# Revit family: QF_BPRO_TRE 6x4_575098
name_source: partatom
category: Sonderausstattung
revit_build: Autodesk Revit 2018 (Build: 20181015_0930(x64)
units: mm (PartAtom-declared; Revit-internal decimal feet)

## family parameters
Arbeitsebenenbasiert = Nein
Beim Laden mit Abzugskörper schneiden = Nein
Bemaßung runder Anschluss = Durchmesser verwenden
Gemeinsam genutzt = Nein
Immer vertikal = Ja
Raumberechnungspunkt = Nein
Teiletyp = Normal

## types (1)
- TRE 6x4
    Artikel Nummer = 575098
    Beschreibung = TRE 6 x 4
Plattformwagen
für Eurobehälter,
inkl. Schiebegriff,
mit umlaufendem Profilrand,
Plattformgröße: 640 x 430 mm
    Beschreibung durch Hersteller analog Leistungsverzeichnislangtext = Abmessungen

Länge:			742 mm
Breite:		430 mm
Höhe:		950 mm
Plattformhöhe:		201 mm


Ausführung

Der Transportroller für Eurobehälter besteht komplett aus CNS 18/10. Die Oberfläche ist mikroliert. 
Stirnseitig befindet sich ein gebogener Schiebegriff aus 25 x 25 mm Vierkantrohr. 

Der Wagen ist fahrbar mittels rostfreien Kunststoffrollen gemäß DIN 18867-8 (4 Lenkrollen, davon 2 mit Feststeller, Rollendurchmesser 125 mm). Stoßleisten aus Kunststoff (Polyethylen) an allen vier Seiten schützen vor Beschädigung.


Technische Daten

Werkstoff:		CNS 18/10
Gewicht:		10 kg 
Gesamttragfähigkeit:	120 kg
Plattformgröße:		600 x 400 mm


Besonderheit

•	Ergonomischer Schiebegriff


Fabrikat

Hersteller:			B.PRO
Modell:	TRE 6 x 4
Best.Nr.	575 098
    CE Kennzeichnung = Ja
    Gerätegewicht Netto = 10.00 kg
    Großküchengerätezuordnung = Ja
    Hersteller = B.PRO GmbH
    Höhe = 950 mm
    Internetadresse Gerätehersteller = https://www.bpro-solutions.com
    Kosten = 391.1 $
    Länge Gerätebreite = 742 mm
    Material = QF_Metal-Stainless-Steel_general
    Material Rollen = QF_Plastic-Dark_Grey-Matt
    Material Stoßschutz = QF_Plastic-Dark_Grey-Matt
    Modell = TRE 6x4
    Tiefe = 430 mm
    Typenkommentare = Transportwagen für Eurobehälter
    URL = https://www.bpro-solutions.com
    Zubehör = Ja
